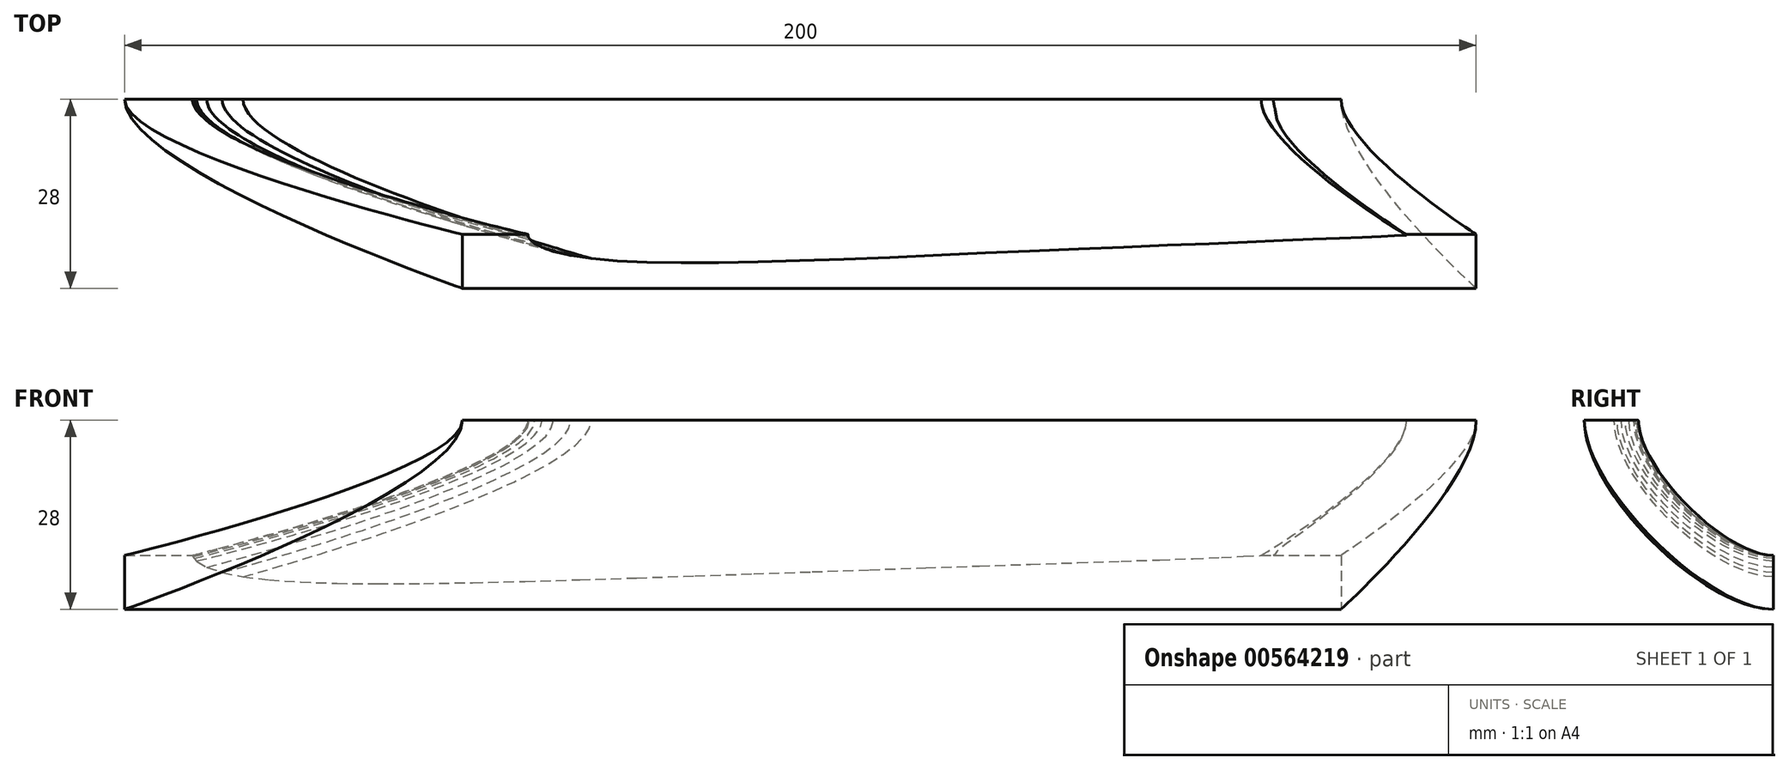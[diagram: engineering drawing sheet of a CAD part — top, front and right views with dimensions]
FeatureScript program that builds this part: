
annotation { "Feature Type Name" : "Feature", "Feature Type Description" : "" }
export const myFeature = defineFeature(function(context is Context, id is Id, definition is map)
    precondition{}
    {
        {
            var Q0;
            Q0=qCreatedBy(makeId("Top.planeOp"),FACE);
            cPlane(context, id + "F0", {"entities" : qUnion([Q0]), "cplaneType" : CPlaneType.OFFSET, "offset" : 20 * mm, "width" : 150 * mm, "height" : 150 * mm});
        }
        {
            var Q0;
            Q0=qCreatedBy(id+"F0.planeOp",FACE);
            var sketch = newSketch(context, id + "F1", { "sketchPlane" : qUnion([Q0])});
            skLineSegment(sketch, "E0", {"start": v(19.7, -19.84) * mm, "end": v(19.16, -19.85) * mm});
            skLineSegment(sketch, "E1", {"start": v(19.16, -19.85) * mm, "end": v(17.98, -19.78) * mm});
            skLineSegment(sketch, "E2", {"start": v(17.98, -19.78) * mm, "end": v(15.76, -19.7) * mm});
            skLineSegment(sketch, "E3", {"start": v(15.76, -19.7) * mm, "end": v(12.9, -19.56) * mm});
            skLineSegment(sketch, "E4", {"start": v(12.9, -19.56) * mm, "end": v(9.15, -19.4) * mm});
            skLineSegment(sketch, "E5", {"start": v(9.15, -19.4) * mm, "end": v(5.03, -19.25) * mm});
            skLineSegment(sketch, "E6", {"start": v(5.03, -19.25) * mm, "end": v(0.59, -19.04) * mm});
            skLineSegment(sketch, "E7", {"start": v(0.59, -19.04) * mm, "end": v(-4.3, -18.86) * mm});
            skLineSegment(sketch, "E8", {"start": v(-4.3, -18.86) * mm, "end": v(-9.93, -18.58) * mm});
            skLineSegment(sketch, "E9", {"start": v(-9.93, -18.58) * mm, "end": v(-15.46, -18.4) * mm});
            skLineSegment(sketch, "E10", {"start": v(-15.46, -18.4) * mm, "end": v(-21.25, -18.11) * mm});
            skLineSegment(sketch, "E11", {"start": v(-21.25, -18.11) * mm, "end": v(-27.83, -17.85) * mm});
            skLineSegment(sketch, "E12", {"start": v(-27.83, -17.85) * mm, "end": v(-34.17, -17.6) * mm});
            skLineSegment(sketch, "E13", {"start": v(-34.17, -17.6) * mm, "end": v(-40.77, -17.32) * mm});
            skLineSegment(sketch, "E14", {"start": v(-40.77, -17.32) * mm, "end": v(-47.7, -16.97) * mm});
            skLineSegment(sketch, "E15", {"start": v(-47.7, -16.97) * mm, "end": v(-53.75, -16.74) * mm});
            skLineSegment(sketch, "E16", {"start": v(-53.75, -16.74) * mm, "end": v(-60.52, -16.43) * mm});
            skLineSegment(sketch, "E17", {"start": v(-60.52, -16.43) * mm, "end": v(-65.14, -16.26) * mm});
            skLineSegment(sketch, "E18", {"start": v(-65.14, -16.26) * mm, "end": v(-71.91, -16.02) * mm});
            skLineSegment(sketch, "E19", {"start": v(-71.91, -16.02) * mm, "end": v(-76.64, -15.9) * mm});
            skLineSegment(sketch, "E20", {"start": v(-76.64, -15.9) * mm, "end": v(-82.29, -15.8) * mm});
            skLineSegment(sketch, "E21", {"start": v(-82.29, -15.8) * mm, "end": v(-87.14, -15.78) * mm});
            skLineSegment(sketch, "E22", {"start": v(-87.14, -15.78) * mm, "end": v(-92, -15.85) * mm});
            skLineSegment(sketch, "E23", {"start": v(-92, -15.85) * mm, "end": v(-95.73, -16) * mm});
            skLineSegment(sketch, "E24", {"start": v(-95.73, -16) * mm, "end": v(-99.09, -16.25) * mm});
            skLineSegment(sketch, "E25", {"start": v(-99.09, -16.25) * mm, "end": v(-102.67, -16.66) * mm});
            skLineSegment(sketch, "E26", {"start": v(-102.67, -16.66) * mm, "end": v(-105.25, -17.11) * mm});
            skLineSegment(sketch, "E27", {"start": v(-105.25, -17.11) * mm, "end": v(-107.38, -17.72) * mm});
            skLineSegment(sketch, "E28", {"start": v(-107.38, -17.72) * mm, "end": v(-108.98, -18.44) * mm});
            skLineSegment(sketch, "E29", {"start": v(-108.98, -18.44) * mm, "end": v(-109.81, -19.02) * mm});
            skLineSegment(sketch, "E30", {"start": v(-109.81, -19.02) * mm, "end": v(-110.22, -19.6) * mm});
            skLineSegment(sketch, "E31", {"start": v(-110.22, -19.6) * mm, "end": v(-110.3, -20) * mm});
            skLineSegment(sketch, "E32", {"start": v(-110.3, -20) * mm, "end": v(-110.27, -20.22) * mm});
            skLineSegment(sketch, "E33", {"start": v(-110.27, -20.22) * mm, "end": v(-110.22, -20.45) * mm});
            skLineSegment(sketch, "E34", {"start": v(-110.22, -20.45) * mm, "end": v(-110.08, -20.67) * mm});
            skLineSegment(sketch, "E35", {"start": v(-110.08, -20.67) * mm, "end": v(-109.3, -21.38) * mm});
            skLineSegment(sketch, "E36", {"start": v(-109.3, -21.38) * mm, "end": v(-108.23, -21.93) * mm});
            skLineSegment(sketch, "E37", {"start": v(-108.23, -21.93) * mm, "end": v(-106.57, -22.53) * mm});
            skLineSegment(sketch, "E38", {"start": v(-106.57, -22.53) * mm, "end": v(-103.96, -23.13) * mm});
            skLineSegment(sketch, "E39", {"start": v(-103.96, -23.13) * mm, "end": v(-100.94, -23.57) * mm});
            skLineSegment(sketch, "E40", {"start": v(-100.94, -23.57) * mm, "end": v(-97.12, -23.91) * mm});
            skLineSegment(sketch, "E41", {"start": v(-97.12, -23.91) * mm, "end": v(-92.73, -24.14) * mm});
            skLineSegment(sketch, "E42", {"start": v(-92.73, -24.14) * mm, "end": v(-87.63, -24.2) * mm});
            skLineSegment(sketch, "E43", {"start": v(-87.63, -24.2) * mm, "end": v(-82.12, -24.22) * mm});
            skLineSegment(sketch, "E44", {"start": v(-82.12, -24.22) * mm, "end": v(-76.28, -24.06) * mm});
            skLineSegment(sketch, "E45", {"start": v(-76.28, -24.06) * mm, "end": v(-70.12, -23.88) * mm});
            skLineSegment(sketch, "E46", {"start": v(-70.12, -23.88) * mm, "end": v(-63.57, -23.67) * mm});
            skLineSegment(sketch, "E47", {"start": v(-63.57, -23.67) * mm, "end": v(-56.78, -23.4) * mm});
            skLineSegment(sketch, "E48", {"start": v(-56.78, -23.4) * mm, "end": v(-49.1, -23.04) * mm});
            skLineSegment(sketch, "E49", {"start": v(-49.1, -23.04) * mm, "end": v(-42.6, -22.76) * mm});
            skLineSegment(sketch, "E50", {"start": v(-42.6, -22.76) * mm, "end": v(-36.05, -22.49) * mm});
            skLineSegment(sketch, "E51", {"start": v(-36.05, -22.49) * mm, "end": v(-28.85, -22.17) * mm});
            skLineSegment(sketch, "E52", {"start": v(-28.85, -22.17) * mm, "end": v(-22.14, -21.9) * mm});
            skLineSegment(sketch, "E53", {"start": v(-22.14, -21.9) * mm, "end": v(-15.69, -21.62) * mm});
            skLineSegment(sketch, "E54", {"start": v(-15.69, -21.62) * mm, "end": v(-9.54, -21.37) * mm});
            skLineSegment(sketch, "E55", {"start": v(-9.54, -21.37) * mm, "end": v(-3.88, -21.13) * mm});
            skLineSegment(sketch, "E56", {"start": v(-3.88, -21.13) * mm, "end": v(1.4, -20.9) * mm});
            skLineSegment(sketch, "E57", {"start": v(1.4, -20.9) * mm, "end": v(5.8, -20.72) * mm});
            skLineSegment(sketch, "E58", {"start": v(5.8, -20.72) * mm, "end": v(9.8, -20.54) * mm});
            skLineSegment(sketch, "E59", {"start": v(9.8, -20.54) * mm, "end": v(13.11, -20.43) * mm});
            skLineSegment(sketch, "E60", {"start": v(13.11, -20.43) * mm, "end": v(15.93, -20.29) * mm});
            skLineSegment(sketch, "E61", {"start": v(15.93, -20.29) * mm, "end": v(17.9, -20.2) * mm});
            skLineSegment(sketch, "E62", {"start": v(17.9, -20.2) * mm, "end": v(19.7, -20.13) * mm});
            skLineSegment(sketch, "E63", {"start": v(19.7, -20.13) * mm, "end": v(19.7, -19.84) * mm});
            skSolve(sketch);
        }
        {
            var Q0;
            Q0=qCreatedBy(makeId("Front.planeOp"),FACE);
            var sketch = newSketch(context, id + "F2", { "sketchPlane" : qUnion([Q0])});
            skLineSegment(sketch, "E64", {"start": v(0, 0.27) * mm, "end": v(-0.56, 0.3) * mm});
            skLineSegment(sketch, "E65", {"start": v(-0.56, 0.3) * mm, "end": v(-2.2, 0.4) * mm});
            skLineSegment(sketch, "E66", {"start": v(-2.2, 0.4) * mm, "end": v(-4.85, 0.64) * mm});
            skLineSegment(sketch, "E67", {"start": v(-4.85, 0.64) * mm, "end": v(-8.43, 1.04) * mm});
            skLineSegment(sketch, "E68", {"start": v(-8.43, 1.04) * mm, "end": v(-12.86, 1.6) * mm});
            skLineSegment(sketch, "E69", {"start": v(-12.86, 1.6) * mm, "end": v(-18.04, 2.29) * mm});
            skLineSegment(sketch, "E70", {"start": v(-18.04, 2.29) * mm, "end": v(-23.9, 3.1) * mm});
            skLineSegment(sketch, "E71", {"start": v(-23.9, 3.1) * mm, "end": v(-30.35, 4.03) * mm});
            skLineSegment(sketch, "E72", {"start": v(-30.35, 4.03) * mm, "end": v(-37.3, 5.02) * mm});
            skLineSegment(sketch, "E73", {"start": v(-37.3, 5.02) * mm, "end": v(-44.65, 6.06) * mm});
            skLineSegment(sketch, "E74", {"start": v(-44.65, 6.06) * mm, "end": v(-52.32, 7.1) * mm});
            skLineSegment(sketch, "E75", {"start": v(-52.32, 7.1) * mm, "end": v(-60.2, 8.12) * mm});
            skLineSegment(sketch, "E76", {"start": v(-60.2, 8.12) * mm, "end": v(-68.23, 9.09) * mm});
            skLineSegment(sketch, "E77", {"start": v(-68.23, 9.09) * mm, "end": v(-76.31, 9.96) * mm});
            skLineSegment(sketch, "E78", {"start": v(-76.31, 9.96) * mm, "end": v(-84.36, 10.71) * mm});
            skLineSegment(sketch, "E79", {"start": v(-84.36, 10.71) * mm, "end": v(-92.3, 11.32) * mm});
            skLineSegment(sketch, "E80", {"start": v(-92.3, 11.32) * mm, "end": v(-100.04, 11.75) * mm});
            skLineSegment(sketch, "E81", {"start": v(-100.04, 11.75) * mm, "end": v(-107.54, 12) * mm});
            skLineSegment(sketch, "E82", {"start": v(-107.54, 12) * mm, "end": v(-114.72, 12.04) * mm});
            skLineSegment(sketch, "E83", {"start": v(-114.72, 12.04) * mm, "end": v(-121.52, 11.88) * mm});
            skLineSegment(sketch, "E84", {"start": v(-121.52, 11.88) * mm, "end": v(-127.88, 11.5) * mm});
            skLineSegment(sketch, "E85", {"start": v(-127.88, 11.5) * mm, "end": v(-133.77, 10.9) * mm});
            skLineSegment(sketch, "E86", {"start": v(-133.77, 10.9) * mm, "end": v(-139.14, 10.1) * mm});
            skLineSegment(sketch, "E87", {"start": v(-139.14, 10.1) * mm, "end": v(-143.97, 9.12) * mm});
            skLineSegment(sketch, "E88", {"start": v(-143.97, 9.12) * mm, "end": v(-148.2, 7.98) * mm});
            skLineSegment(sketch, "E89", {"start": v(-148.2, 7.98) * mm, "end": v(-151.82, 6.73) * mm});
            skLineSegment(sketch, "E90", {"start": v(-151.82, 6.73) * mm, "end": v(-154.8, 5.38) * mm});
            skLineSegment(sketch, "E91", {"start": v(-154.8, 5.38) * mm, "end": v(-157.13, 4) * mm});
            skLineSegment(sketch, "E92", {"start": v(-157.13, 4) * mm, "end": v(-158.77, 2.6) * mm});
            skLineSegment(sketch, "E93", {"start": v(-158.77, 2.6) * mm, "end": v(-159.73, 1.27) * mm});
            skLineSegment(sketch, "E94", {"start": v(-159.73, 1.27) * mm, "end": v(-159.97, 0.57) * mm});
            skLineSegment(sketch, "E95", {"start": v(-159.97, 0.57) * mm, "end": v(-160, 0.3) * mm});
            skLineSegment(sketch, "E96", {"start": v(-160, 0.3) * mm, "end": v(-159.98, 0.04) * mm});
            skLineSegment(sketch, "E97", {"start": v(-159.98, 0.04) * mm, "end": v(-159.89, -0.2) * mm});
            skLineSegment(sketch, "E98", {"start": v(-159.89, -0.2) * mm, "end": v(-159.73, -0.44) * mm});
            skLineSegment(sketch, "E99", {"start": v(-159.73, -0.44) * mm, "end": v(-159.34, -0.86) * mm});
            skLineSegment(sketch, "E100", {"start": v(-159.34, -0.86) * mm, "end": v(-157.85, -1.76) * mm});
            skLineSegment(sketch, "E101", {"start": v(-157.85, -1.76) * mm, "end": v(-155.56, -2.55) * mm});
            skLineSegment(sketch, "E102", {"start": v(-155.56, -2.55) * mm, "end": v(-152.48, -3.18) * mm});
            skLineSegment(sketch, "E103", {"start": v(-152.48, -3.18) * mm, "end": v(-148.6, -3.65) * mm});
            skLineSegment(sketch, "E104", {"start": v(-148.6, -3.65) * mm, "end": v(-143.95, -3.96) * mm});
            skLineSegment(sketch, "E105", {"start": v(-143.95, -3.96) * mm, "end": v(-138.56, -4.14) * mm});
            skLineSegment(sketch, "E106", {"start": v(-138.56, -4.14) * mm, "end": v(-132.48, -4.2) * mm});
            skLineSegment(sketch, "E107", {"start": v(-132.48, -4.2) * mm, "end": v(-125.76, -4.16) * mm});
            skLineSegment(sketch, "E108", {"start": v(-125.76, -4.16) * mm, "end": v(-118.5, -4.04) * mm});
            skLineSegment(sketch, "E109", {"start": v(-118.5, -4.04) * mm, "end": v(-110.75, -3.85) * mm});
            skLineSegment(sketch, "E110", {"start": v(-110.75, -3.85) * mm, "end": v(-102.62, -3.61) * mm});
            skLineSegment(sketch, "E111", {"start": v(-102.62, -3.61) * mm, "end": v(-94.21, -3.34) * mm});
            skLineSegment(sketch, "E112", {"start": v(-94.21, -3.34) * mm, "end": v(-85.61, -3.05) * mm});
            skLineSegment(sketch, "E113", {"start": v(-85.61, -3.05) * mm, "end": v(-76.93, -2.74) * mm});
            skLineSegment(sketch, "E114", {"start": v(-76.93, -2.74) * mm, "end": v(-68.27, -2.44) * mm});
            skLineSegment(sketch, "E115", {"start": v(-68.27, -2.44) * mm, "end": v(-59.74, -2.14) * mm});
            skLineSegment(sketch, "E116", {"start": v(-59.74, -2.14) * mm, "end": v(-51.45, -1.85) * mm});
            skLineSegment(sketch, "E117", {"start": v(-51.45, -1.85) * mm, "end": v(-43.49, -1.58) * mm});
            skLineSegment(sketch, "E118", {"start": v(-43.49, -1.58) * mm, "end": v(-35.95, -1.32) * mm});
            skLineSegment(sketch, "E119", {"start": v(-35.95, -1.32) * mm, "end": v(-28.94, -1.08) * mm});
            skLineSegment(sketch, "E120", {"start": v(-28.94, -1.08) * mm, "end": v(-22.53, -0.87) * mm});
            skLineSegment(sketch, "E121", {"start": v(-22.53, -0.87) * mm, "end": v(-16.82, -0.67) * mm});
            skLineSegment(sketch, "E122", {"start": v(-16.82, -0.67) * mm, "end": v(-11.85, -0.48) * mm});
            skLineSegment(sketch, "E123", {"start": v(-11.85, -0.48) * mm, "end": v(-7.7, -0.3) * mm});
            skLineSegment(sketch, "E124", {"start": v(-7.7, -0.3) * mm, "end": v(-4.43, -0.13) * mm});
            skLineSegment(sketch, "E125", {"start": v(-4.43, -0.13) * mm, "end": v(-1.86, -0.02) * mm});
            skLineSegment(sketch, "E126", {"start": v(-1.86, -0.02) * mm, "end": v(0, 0) * mm});
            skLineSegment(sketch, "E127", {"start": v(0, 0) * mm, "end": v(0, 0.27) * mm});
            skSolve(sketch);
        }
        {
            var Q0;
            Q0=qSketchRegion(id+"F2",true);
            var Q1;
            Q1=qSketchRegion(id+"F1",true);
            loft(context, id + "F3", {"startCondition" : LoftEndDerivativeType.NORMAL_TO_PROFILE, "startMagnitude" : 1, "endCondition" : LoftEndDerivativeType.NORMAL_TO_PROFILE, "endMagnitude" : 1, "sheetProfilesArray" : [{ "sheetProfileEntities" : qUnion([Q0]) }, { "sheetProfileEntities" : qUnion([Q1]) }]});
        }
        {
            var Q0;
            Q0=qCreatedBy(id+"F0.planeOp",FACE);
            var sketch = newSketch(context, id + "F4", { "sketchPlane" : qUnion([Q0])});
            skLineSegment(sketch, "E128.bottom", {"start": v(-120, -20) * mm, "end": v(30, -20) * mm});
            skLineSegment(sketch, "E128.top", {"start": v(-120, -28) * mm, "end": v(30, -28) * mm});
            skLineSegment(sketch, "E128.left", {"start": v(-120, -20) * mm, "end": v(-120, -28) * mm});
            skLineSegment(sketch, "E128.right", {"start": v(30, -20) * mm, "end": v(30, -28) * mm});
            skSolve(sketch);
        }
        {
            var Q0;
            Q0=qCreatedBy(makeId("Front.planeOp"),FACE);
            var sketch = newSketch(context, id + "F5", { "sketchPlane" : qUnion([Q0])});
            skLineSegment(sketch, "E129.bottom", {"start": v(-170, 0) * mm, "end": v(10, 0) * mm});
            skLineSegment(sketch, "E129.top", {"start": v(-170, -8) * mm, "end": v(10, -8) * mm});
            skLineSegment(sketch, "E129.left", {"start": v(-170, 0) * mm, "end": v(-170, -8) * mm});
            skLineSegment(sketch, "E129.right", {"start": v(10, 0) * mm, "end": v(10, -8) * mm});
            skSolve(sketch);
        }
        {
            var Q1;
            Q1 = qSketchRegion(id + "F4", true);
            var Q2;
            Q2 = qSketchRegion(id + "F5", true);
            loft(context, id + "F6", {"startCondition" : LoftEndDerivativeType.NORMAL_TO_PROFILE, "startMagnitude" : 1, "endCondition" : LoftEndDerivativeType.NORMAL_TO_PROFILE, "endMagnitude" : 1, "sheetProfilesArray" : [{ "sheetProfileEntities" : qUnion([Q1]) }, { "sheetProfileEntities" : qUnion([Q2]) }]});
        }
        {
            var Q0;
            Q0=makeQuery(id+"F3.opLoft","SWEPT_BODY",BODY,{"disambiguationData":[OSD([makeQuery(id+"F1.imprint","IMPRINT",FACE,{"disambiguationData":[TD([[makeQuery(id+"F1.imprint","IMPRINT",EDGE,{"derivedFrom":sQuery(id+"F1.wireOp",EDGE,"E0")}),1.0]])]}),makeQuery(id+"F2.imprint","IMPRINT",FACE,{"disambiguationData":[TD([[makeQuery(id+"F2.imprint","IMPRINT",EDGE,{"derivedFrom":sQuery(id+"F2.wireOp",EDGE,"E64")}),1.0]])]})])]});
            var Q1;
            Q1=makeQuery(id+"F6.opLoft","SWEPT_BODY",BODY,{"disambiguationData":[OSD([makeQuery(id+"F4.imprint","IMPRINT",FACE,{"disambiguationData":[TD([[makeQuery(id+"F4.imprint","IMPRINT",EDGE,{"derivedFrom":sQuery(id+"F4.wireOp",EDGE,"E128.bottom")}),-1.0]])]}),makeQuery(id+"F5.imprint","IMPRINT",FACE,{"disambiguationData":[TD([[makeQuery(id+"F5.imprint","IMPRINT",EDGE,{"derivedFrom":sQuery(id+"F5.wireOp",EDGE,"E129.bottom")}),-1.0]])]})])]});
            booleanBodies(context, id + "F7", {"operationType" : BooleanOperationType.SUBTRACTION, "tools" : qUnion([Q0]), "targets" : qUnion([Q1])});
        }
    });
